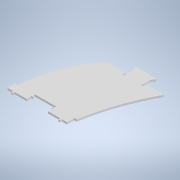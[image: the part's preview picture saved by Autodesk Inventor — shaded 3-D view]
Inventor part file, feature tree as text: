
AUTODESK INVENTOR PART (.ipt)
format: ipt  version: 2020 (Build 240168000, 168)  size: 303,104 bytes
history: native  units: mm
features: extrude x1, sketch x1
ambient origin geometry x8: Origin, YZ Plane, XZ Plane, XY Plane, X Axis, Y Axis, Z Axis, Center Point
bodies: Body1 (feature_tree)
feature tree (2):
  extrude  "Extrusion4"  Depth=658.71mm
  sketch  "Sketch1"  dims[d99=181.29mm d102=2.666667mm d105=32.04mm d106=10.0mm d107=2.666667mm d108=6.5mm d109=2.666667mm d141=7.333333mm d142=5.0mm d170=13.004821mm d173=6.0mm d174=5.5mm d177=7.5mm d179=2.666667mm d181=232.826mm d183=264.8664mm d184=23.330082mm d186=57.3335mm d187=57.3335mm d189=6.5mm d190=7.333333mm d191=24.187002mm d192=1.333333mm d193=6.0mm d194=0.0mm d202=6.0mm d203=1.333333mm d204=1.333333mm d208=191.29mm d209=2.666667mm d210=2.666667mm d211=14.47956mm d212=14.47956mm d213=61.341583mm d214=145.0mm d216=23.333333mm d217=7.5mm d220=7.5mm d221=2.666667mm d223=38.198366mm d226=61.341583mm d232=2.666667mm d233=2.666667mm d234=61.341583mm d235=60.0deg d236=33.288886mm d237=2.0mm d238=425.0mm d239=658.71mm d195=0.872665mm]
